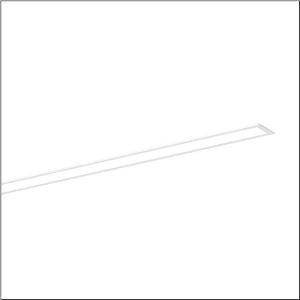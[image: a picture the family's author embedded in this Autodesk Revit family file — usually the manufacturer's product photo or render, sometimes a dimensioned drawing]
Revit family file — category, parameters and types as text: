
# Revit family: silica_r__21_51mx10tat2w_99a0
name_source: partatom
category: Lighting Fixtures
units: mm (PartAtom-declared; Revit-internal decimal feet)

## family parameters
Cut with Voids When Loaded = No
Host = Face
Light Source = No
Part Type = Normal
Room Calculation Point = No
Round Connector Dimension = Use Diameter
Shared = No

## types (1)
- --- (1 x LED, 2400 lm, 20.5 W, 6500K)
    Apparent Load = 21 VA
    CIE Flux Codes = 48 79 96 100 100
    Color Rendering = 80
    Color Temperature = 6500K
    Default Elevation = 1800 mm
    Description = Silica® 21, office luminaire, primary optical cover: cover, of PMMA, opal, light emission: direct distribution, primary light characteristic: symmetric, installation type: recessed, LED, rated luminous flux: 2.400lm, luminous efficacy: 112lm/W, light colour: 8tw, colour temperature: 2700..6500K, with terminal, 3+2-pole, max. 2.5mm², mains connection: 220..240V, AC, 50/60Hz, rated input power: 21.5W, luminaire housing, of aluminium, traffic white (RAL 9016), length: 1.228mm, width: 79mm, height: 53mm, protection rating (complete): IP20, insulation class (complete): insulation class I (protective earthing), certification: CE, permissible operating ambient temperature: 0..+35°C, standard: EN 50419, packaging unit: 1 piece
    Height = 0 mm  [stored 0 ft]
    Lamp = 1 x LED
    Lamp Light Flux = 2400 lm
    Lamp Power = 20.5 W
    Lamp count = 1
    Length = 1227 mm
    Luminous efficacy = 117 lm/W
    Manufacturer = Siteco
    ModVariant = No
    Model = 51MX10TAT2W
    Mounting Place = Ceiling
    Mounting Type = Recessed
    Number of Poles = 1
    OnlyDefault = Yes
    Power Factor = 1
    Product Name = Silica® 21
    Product group = office luminaire | ceiling recessed
    ProductGroupID = 401
    Protection Class = Protection class I
    Protection Degree = IP 20
    RLX_Detail_Level = 1
    RLX_Emergency_Light_Flux = 0 lm
    RLX_Emergency_Type = 0
    RLX_Emergency_Type_DB = No
    RlxData = <blob elided: 17865 chars, md5=6ff322c2>
    Socket = socket
    Standby Power = 0 W
    System Light Flux = 2400 lm
    System Power = 21 W
    Type Comments = individual setting
    Type Image = l_1313615.jpg
    URL = http://relux.com
    VarID = @adj_089097
    Voltage = 0 V
    Weight = 0.00 kg
    Width = 79 mm

note: [stored X ft] marks values corroborated as IEEE doubles in the binary element streams (Revit-internal decimal feet)

## geometry (parser evidence)
native form markers: Blend x4, Sweep x13
no freeform markers — native parametric forms only
